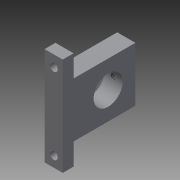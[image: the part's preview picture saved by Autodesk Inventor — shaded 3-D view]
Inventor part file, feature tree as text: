
AUTODESK INVENTOR PART (.ipt)
format: ipt  version: 2014 SP2 (Build 180246200, 246)  size: 119,808 bytes
history: native  units: mm
features: other x7, sketch x4, hole x3, extrude x1, pattern_linear x1
ambient origin geometry x8: Origin, YZ Plane, XZ Plane, XY Plane, X Axis, Y Axis, Z Axis, Center Point
bodies: Solid1 (feature_tree)
feature tree (16):
  extrude  "Extrusion1"  Depth=10.0mm TaperAngle=0.0deg
  hole  "Hole1"  [1 undecoded]
  hole  "Hole2"  [1 undecoded]
  pattern_linear  "Rectangular Pattern1"  [2 undecoded]
  hole  "Hole3"  [1 undecoded]
  other  "b_s_XY"
  other  "b_s_YZ"
  other  "b_s_ZX"
  other  "b_s_X"
  other  "b_s_Y"
  other  "b_s_Z"
  other  "b_s_Center"
  sketch  "Sketch_1"  dims[d0=10.0mm d1=0.0mm]
  sketch  "Sketch2"  dims[d2=3.242mm d3=7.379mm d4=4.0mm d5=2.0mm d6=90.0deg d7=14.064115mm d8=120.0deg]
  sketch  "Sketch3"  dims[d9=4.5mm d10=6.0mm d11=4.0mm d12=2.0mm d13=90.0deg d14=6.0mm d15=0.0mm d16=20.0mm d18=42.0mm d19=10.0mm d21=0.0mm]
  sketch  "Sketch4"  dims[d22=16.0mm d23=6.0mm d24=4.0mm d25=2.0mm d26=90.0deg d27=10.0mm d28=0.0mm]
note: 5 required parameter values undecoded (feature->parameter linkage not recoverable at this tier; creation-order binding heuristic only, values carry confidence <= 0.55)
